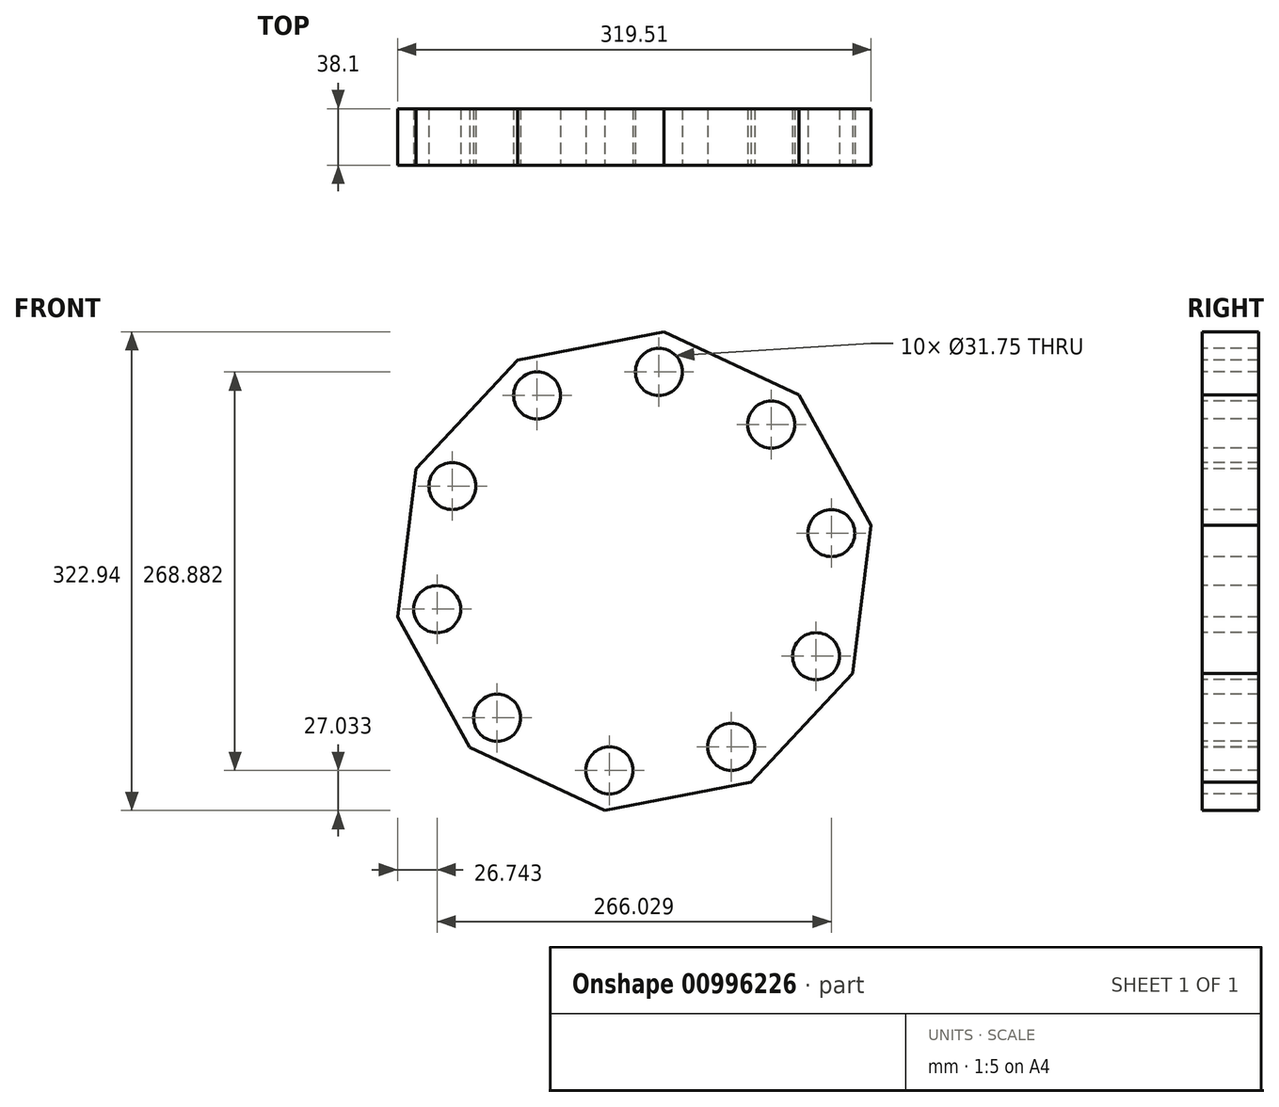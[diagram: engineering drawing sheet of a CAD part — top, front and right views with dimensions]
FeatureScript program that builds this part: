
annotation { "Feature Type Name" : "Feature", "Feature Type Description" : "" }
export const myFeature = defineFeature(function(context is Context, id is Id, definition is map)
    precondition{}
    {
        {
            var Q0;
            Q0=qCreatedBy(makeId("Front.planeOp"),FACE);
            var sketch = newSketch(context, id + "F0", { "sketchPlane" : qUnion([Q0])});
            skCircle(sketch, "E0.cCircle", {"center": v(-54.5, 52.47) * mm, "radius": 154.74 * mm, "construction": true});
            skLineSegment(sketch, "E0.0", {"start": v(92.87, -16.47) * mm, "end": v(24.2, -89.93) * mm});
            skLineSegment(sketch, "E0.1", {"start": v(24.2, -89.93) * mm, "end": v(-74.53, -109) * mm});
            skLineSegment(sketch, "E0.2", {"start": v(-74.53, -109) * mm, "end": v(-165.62, -66.38) * mm});
            skLineSegment(sketch, "E0.3", {"start": v(-165.62, -66.38) * mm, "end": v(-214.26, 21.63) * mm});
            skLineSegment(sketch, "E0.4", {"start": v(-214.26, 21.63) * mm, "end": v(-201.88, 121.42) * mm});
            skLineSegment(sketch, "E0.5", {"start": v(-201.88, 121.42) * mm, "end": v(-133.2, 194.88) * mm});
            skLineSegment(sketch, "E0.6", {"start": v(-133.2, 194.88) * mm, "end": v(-34.47, 213.94) * mm});
            skLineSegment(sketch, "E0.7", {"start": v(-34.47, 213.94) * mm, "end": v(56.61, 171.33) * mm});
            skLineSegment(sketch, "E0.8", {"start": v(56.61, 171.33) * mm, "end": v(105.25, 83.32) * mm});
            skLineSegment(sketch, "E0.9", {"start": v(105.25, 83.32) * mm, "end": v(92.87, -16.47) * mm});
            skPoint(sketch, "E0.0.midPoint", {"position": v(58.54, -53.2) * mm});
            skLineSegment(sketch, "E1", {"start": v(-34.47, 213.94) * mm, "end": v(-74.53, -109) * mm, "construction": true});
            skLineSegment(sketch, "E2", {"start": v(-133.2, 194.88) * mm, "end": v(24.2, -89.93) * mm, "construction": true});
            skLineSegment(sketch, "E3", {"start": v(-201.88, 121.42) * mm, "end": v(92.87, -16.47) * mm, "construction": true});
            skLineSegment(sketch, "E4", {"start": v(-165.62, -66.38) * mm, "end": v(56.61, 171.33) * mm, "construction": true});
            skLineSegment(sketch, "E5", {"start": v(-214.26, 21.63) * mm, "end": v(105.25, 83.32) * mm, "construction": true});
            skCircle(sketch, "E6", {"center": v(-54.5, 52.47) * mm, "radius": 135.47 * mm, "construction": true});
            skCircle(sketch, "E7", {"center": v(-120.03, 171.04) * mm, "radius": 15.88 * mm});
            skCircle(sketch, "E8", {"center": v(-37.83, 186.91) * mm, "radius": 15.88 * mm});
            skCircle(sketch, "E9", {"center": v(38.01, 151.44) * mm, "radius": 15.88 * mm});
            skCircle(sketch, "E10", {"center": v(78.51, 78.16) * mm, "radius": 15.88 * mm});
            skCircle(sketch, "E11", {"center": v(-177.21, 109.88) * mm, "radius": 15.88 * mm});
            skCircle(sketch, "E12", {"center": v(-187.52, 26.8) * mm, "radius": 15.88 * mm});
            skCircle(sketch, "E13", {"center": v(-147.02, -46.49) * mm, "radius": 15.88 * mm});
            skCircle(sketch, "E14", {"center": v(-71.18, -81.97) * mm, "radius": 15.88 * mm});
            skCircle(sketch, "E15", {"center": v(11.03, -66.1) * mm, "radius": 15.88 * mm});
            skCircle(sketch, "E16", {"center": v(68.2, -4.93) * mm, "radius": 15.88 * mm});
            skSolve(sketch);
        }
        {
            var Q0;
            Q0 = qSketchRegion(id + "F0", true);
            extrude(context, id + "F1", {"entities" : qUnion([Q0]), "oppositeDirection" : true, "depth" : 38.1 * mm, "offsetDistance" : 25.4 * mm});
        }
    });
